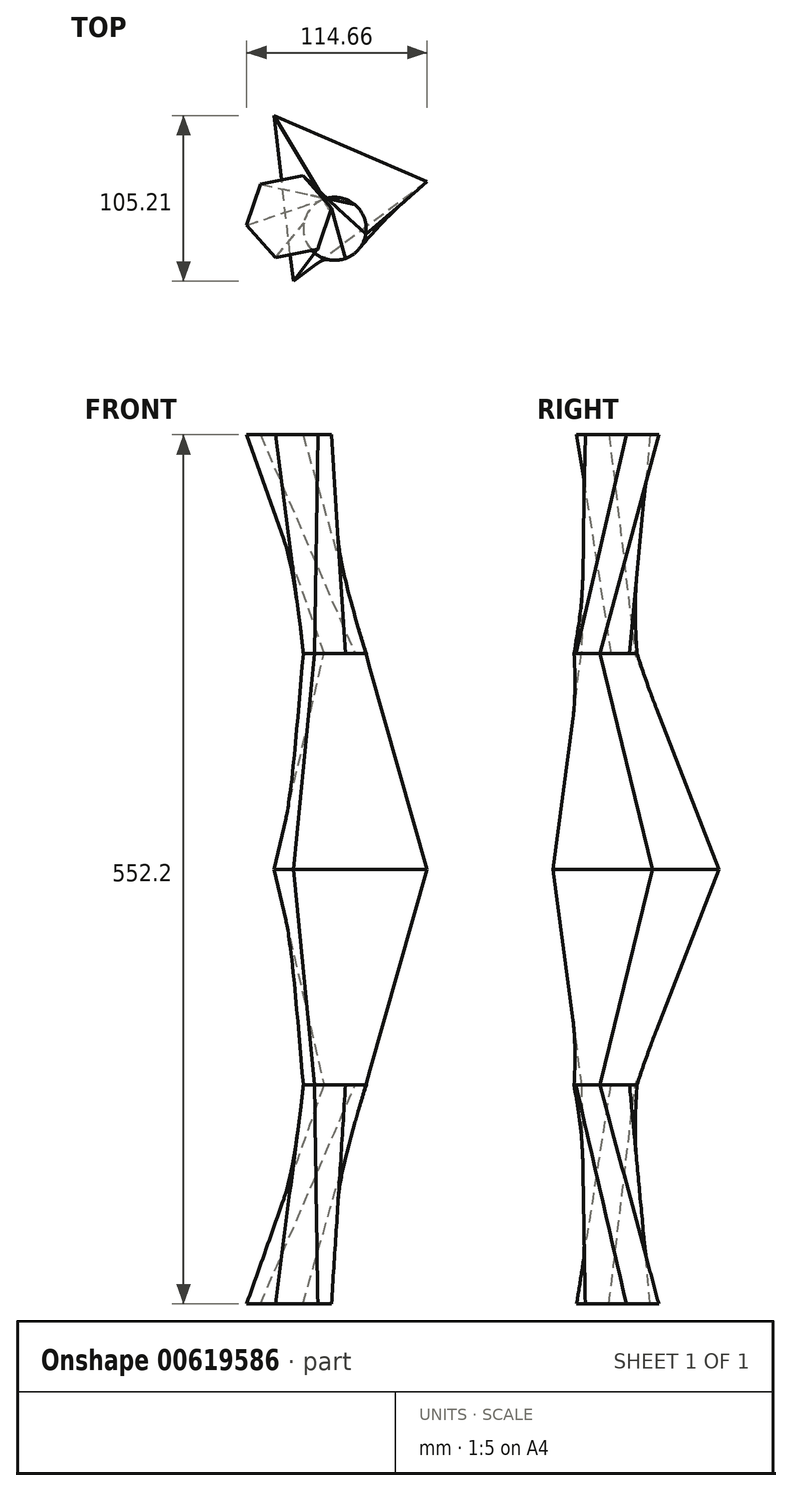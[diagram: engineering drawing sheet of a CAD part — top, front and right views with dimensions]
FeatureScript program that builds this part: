
annotation { "Feature Type Name" : "Feature", "Feature Type Description" : "" }
export const myFeature = defineFeature(function(context is Context, id is Id, definition is map)
    precondition{}
    {
        {
            var Q0;
            Q0=qCreatedBy(makeId("Top.planeOp"),FACE);
            var sketch = newSketch(context, id + "F0", { "sketchPlane" : qUnion([Q0])});
            skCircle(sketch, "E0", {"center": v(0, 0) * mm, "radius": 20 * mm});
            skSolve(sketch);
        }
        {
            var Q0;
            Q0=qCreatedBy(makeId("Top.planeOp"),FACE);
            cPlane(context, id + "F1", {"entities" : qUnion([Q0]), "cplaneType" : CPlaneType.OFFSET, "offset" : 139.1 * mm, "width" : 150 * mm, "height" : 150 * mm});
        }
        {
            var Q0;
            Q0=qCreatedBy(id+"F1.planeOp",FACE);
            var sketch = newSketch(context, id + "F2", { "sketchPlane" : qUnion([Q0])});
            skCircle(sketch, "E1.cCircle", {"center": v(-29.03, 7.75) * mm, "radius": 23.82 * mm, "construction": true});
            skLineSegment(sketch, "E1.0", {"start": v(-10.8, -12.84) * mm, "end": v(-37.75, -18.33) * mm});
            skLineSegment(sketch, "E1.1", {"start": v(-37.75, -18.33) * mm, "end": v(-55.97, 2.27) * mm});
            skLineSegment(sketch, "E1.2", {"start": v(-55.97, 2.27) * mm, "end": v(-47.25, 28.35) * mm});
            skLineSegment(sketch, "E1.3", {"start": v(-47.25, 28.35) * mm, "end": v(-20.3, 33.84) * mm});
            skLineSegment(sketch, "E1.4", {"start": v(-20.3, 33.84) * mm, "end": v(-2.08, 13.24) * mm});
            skLineSegment(sketch, "E1.5", {"start": v(-2.08, 13.24) * mm, "end": v(-10.8, -12.84) * mm});
            skPoint(sketch, "E1.0.midPoint", {"position": v(-24.27, -15.58) * mm});
            skSolve(sketch);
        }
        {
            var Q0;
            Q0=makeQuery(id+"F2.imprint","IMPRINT",FACE,{"disambiguationData":[TD([[makeQuery(id+"F2.imprint","IMPRINT",EDGE,{"derivedFrom":sQuery(id+"F2.wireOp",EDGE,"E1.0")}),-1.0]])]});
            var Q1;
            Q1=makeQuery(id+"F0.imprint","IMPRINT",FACE,{"disambiguationData":[TD([[makeQuery(id+"F0.imprint","IMPRINT",EDGE,{"derivedFrom":sQuery(id+"F0.wireOp",EDGE,"E0")}),1.0]])]});
            loft(context, id + "F3", {"sheetProfilesArray" : [{ "sheetProfileEntities" : qUnion([Q0]) }, { "sheetProfileEntities" : qUnion([Q1]) }]});
        }
        {
            var Q0;
            Q0=qCreatedBy(makeId("Top.planeOp"),FACE);
            cPlane(context, id + "F4", {"entities" : qUnion([Q0]), "cplaneType" : CPlaneType.OFFSET, "offset" : 137 * mm, "oppositeDirection" : true, "width" : 150 * mm, "height" : 150 * mm});
        }
        {
            var Q0;
            Q0=qCreatedBy(id+"F4.planeOp",FACE);
            var sketch = newSketch(context, id + "F5", { "sketchPlane" : qUnion([Q0])});
            skCircle(sketch, "E2.cCircle", {"center": v(-2.05, 22.88) * mm, "radius": 30.57 * mm, "construction": true});
            skLineSegment(sketch, "E2.0", {"start": v(-26.32, -33.25) * mm, "end": v(-38.52, 71.96) * mm});
            skLineSegment(sketch, "E2.1", {"start": v(-38.52, 71.96) * mm, "end": v(58.7, 29.93) * mm});
            skLineSegment(sketch, "E2.2", {"start": v(58.7, 29.93) * mm, "end": v(-26.32, -33.25) * mm});
            skPoint(sketch, "E2.0.midPoint", {"position": v(-32.42, 19.36) * mm});
            skSolve(sketch);
        }
        {
            var Q1;
            Q1=makeQuery(id+"F5.imprint","IMPRINT",FACE,{"disambiguationData":[TD([[makeQuery(id+"F5.imprint","IMPRINT",EDGE,{"derivedFrom":sQuery(id+"F5.wireOp",EDGE,"E2.0")}),-1.0]])]});
            var Q2;
            Q2=makeQuery(id+"F3.opLoft","CAP_FACE",FACE,{"disambiguationData":[OSD([makeQuery(id+"F0.imprint","IMPRINT",FACE,{"disambiguationData":[TD([[makeQuery(id+"F0.imprint","IMPRINT",EDGE,{"derivedFrom":sQuery(id+"F0.wireOp",EDGE,"E0")}),1.0]])]})])],"isStart":true});
            loft(context, id + "F6", {"operationType" : NewBodyOperationType.ADD, "sheetProfilesArray" : [{ "sheetProfileEntities" : qUnion([Q1]) }, { "sheetProfileEntities" : qUnion([Q2]) }]});
        }
        {
            var Q0;
            Q0=makeQuery(id+"F3.opLoft","SWEPT_BODY",BODY,{"disambiguationData":[OSD([makeQuery(id+"F0.imprint","IMPRINT",FACE,{"disambiguationData":[TD([[makeQuery(id+"F0.imprint","IMPRINT",EDGE,{"derivedFrom":sQuery(id+"F0.wireOp",EDGE,"E0")}),1.0]])]}),makeQuery(id+"F2.imprint","IMPRINT",FACE,{"disambiguationData":[TD([[makeQuery(id+"F2.imprint","IMPRINT",EDGE,{"derivedFrom":sQuery(id+"F2.wireOp",EDGE,"E1.0")}),-1.0]])]})])]});
            var Q1;
            Q1=qCreatedBy(id+"F4.planeOp",FACE);
            mirror(context, id + "F7", {"operationType" : NewBodyOperationType.ADD, "entities" : qUnion([Q0]), "mirrorPlane" : qUnion([Q1])});
        }
    });
